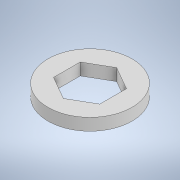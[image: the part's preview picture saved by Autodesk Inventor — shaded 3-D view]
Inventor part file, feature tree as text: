
AUTODESK INVENTOR PART (.ipt)
format: ipt  version: 2022.2 (Build 262287010, 287A)  size: 108,544 bytes
history: native  units: in
note: dims shown in document units (in); Inventor stores cm internally (conversion verified against a paired STEP export)
features: extrude x1, sketch x1
ambient origin geometry x8: Origin, YZ Plane, XZ Plane, XY Plane, X Axis, Y Axis, Z Axis, Center Point
bodies: Solid1 (feature_tree)
feature tree (2):
  extrude  "Extrusion1"  Depth=0.1in
  sketch  "Sketch1"  dims[d0=0.385in d1=0.7in d2=0.1in d3=0.0in]
